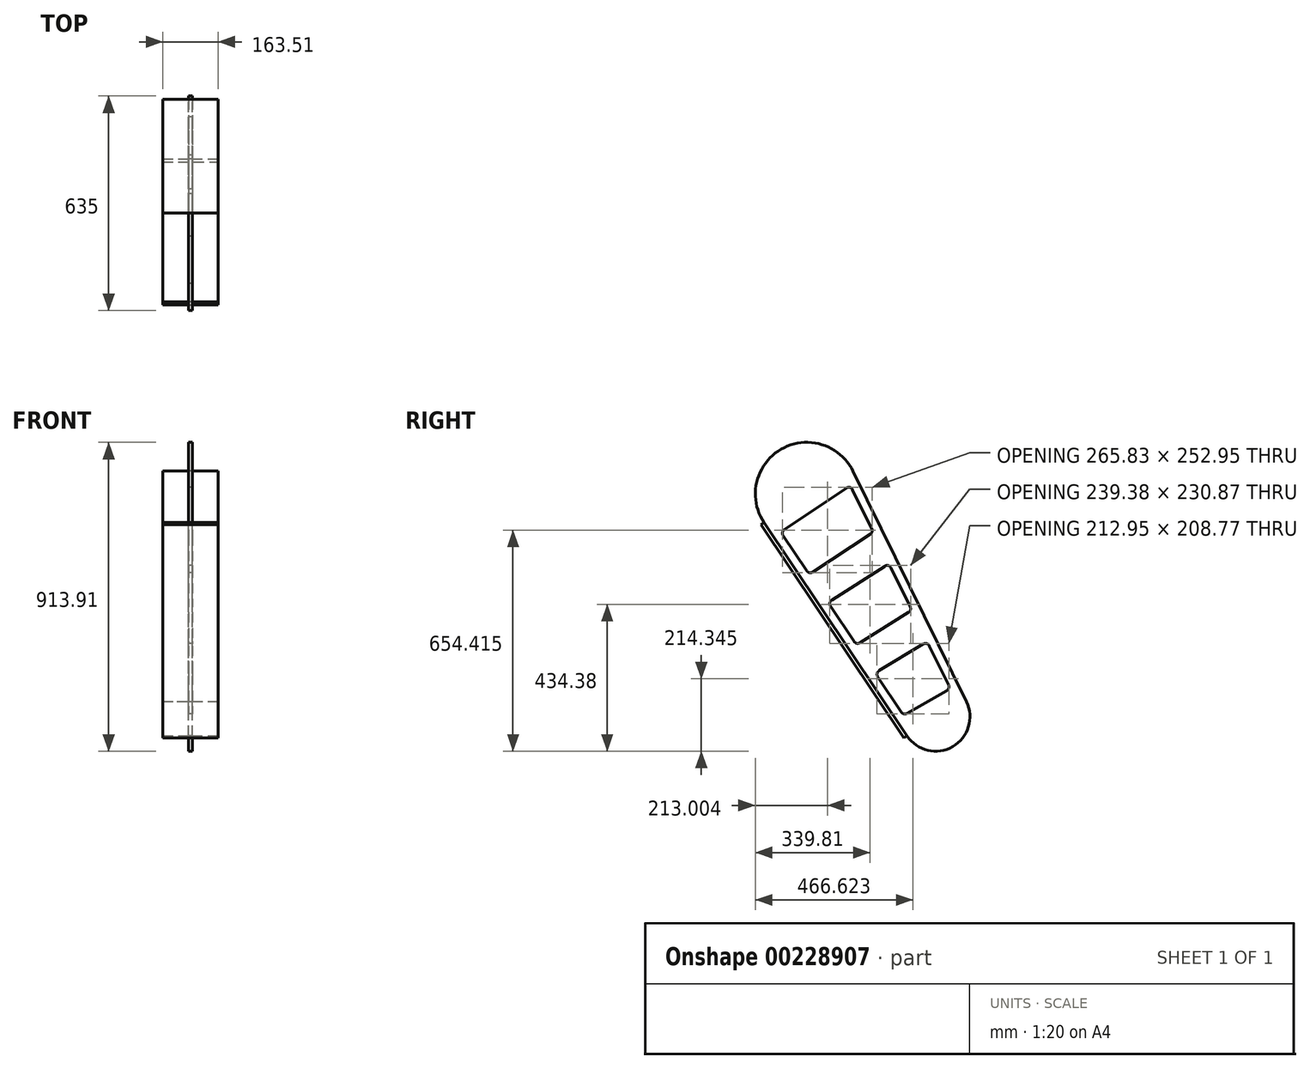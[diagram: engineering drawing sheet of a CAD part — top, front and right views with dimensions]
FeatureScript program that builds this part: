
annotation { "Feature Type Name" : "Feature", "Feature Type Description" : "" }
export const myFeature = defineFeature(function(context is Context, id is Id, definition is map)
    precondition{}
    {
        {
            var Q0;
            Q0=qCreatedBy(makeId("Right.planeOp"),FACE);
            var sketch = newSketch(context, id + "F0", { "sketchPlane" : qUnion([Q0])});
            skCircle(sketch, "E0", {"center": v(-381, 863.11) * mm, "radius": 152.4 * mm, "construction": true});
            skCircle(sketch, "E1", {"center": v(0, 203.2) * mm, "radius": 101.6 * mm, "construction": true});
            skLineSegment(sketch, "E2", {"start": v(91.18, 248.02) * mm, "end": v(-244.23, 930.34) * mm});
            skLineSegment(sketch, "E3", {"start": v(-84.4, 146.65) * mm, "end": v(-507.6, 778.28) * mm});
            skArc(sketch, "E4", {"start": v(-244.23, 930.34) * mm, "mid": v(-457.2, 995.1) * mm, "end": v(-507.6, 778.28) * mm});
            skArc(sketch, "E5", {"start": v(-84.4, 146.65) * mm, "mid": v(50.8, 115.21) * mm, "end": v(91.18, 248.02) * mm});
            skLineSegment(sketch, "E6", {"start": v(-381, 863.11) * mm, "end": v(0, 203.2) * mm, "construction": true});
            skLineSegment(sketch, "E7", {"start": v(-381, 863.11) * mm, "end": v(-228.6, 863.11) * mm, "construction": true});
            skSolve(sketch);
        }
        {
            var Q0;
            Q0=makeQuery(id+"F0.imprint","IMPRINT",FACE,{"disambiguationData":[TD([[makeQuery(id+"F0.imprint","IMPRINT",EDGE,{"derivedFrom":sQuery(id+"F0.wireOp",EDGE,"E2")}),1.0]])]});
            var sketch = newSketch(context, id + "F1", { "sketchPlane" : qUnion([Q0])});
            skArc(sketch, "E8.0", {"start": v(-244.23, 930.34) * mm, "mid": v(-457.2, 995.1) * mm, "end": v(-507.6, 778.28) * mm});
            skLineSegment(sketch, "E8.1", {"start": v(91.18, 248.02) * mm, "end": v(-244.23, 930.34) * mm});
            skArc(sketch, "E8.2", {"start": v(-84.4, 146.65) * mm, "mid": v(50.8, 115.21) * mm, "end": v(91.18, 248.02) * mm});
            skLineSegment(sketch, "E8.3", {"start": v(-84.4, 146.65) * mm, "end": v(-507.6, 778.28) * mm});
            skCircle(sketch, "E9", {"center": v(-440.61, 746.74) * mm, "radius": 12.7 * mm, "construction": true});
            skLineSegment(sketch, "E10", {"start": v(-440.61, 746.74) * mm, "end": v(-90.54, 224.25) * mm, "construction": true});
            skCircle(sketch, "E11.1.0.0", {"center": v(-370.6, 642.24) * mm, "radius": 12.7 * mm, "construction": true});
            skCircle(sketch, "E11.2.0.0", {"center": v(-300.58, 537.74) * mm, "radius": 12.7 * mm, "construction": true});
            skCircle(sketch, "E11.3.0.0", {"center": v(-230.57, 433.24) * mm, "radius": 12.7 * mm, "construction": true});
            skCircle(sketch, "E11.4.0.0", {"center": v(-160.55, 328.75) * mm, "radius": 12.7 * mm, "construction": true});
            skCircle(sketch, "E11.5.0.0", {"center": v(-90.54, 224.25) * mm, "radius": 12.7 * mm, "construction": true});
            skLineSegment(sketch, "E11.direction1", {"start": v(-440.61, 746.74) * mm, "end": v(-370.6, 642.24) * mm, "construction": true});
            skCircle(sketch, "E12", {"center": v(-256.93, 869.8) * mm, "radius": 12.7 * mm, "construction": true});
            skLineSegment(sketch, "E13", {"start": v(-440.61, 746.74) * mm, "end": v(-256.93, 869.8) * mm, "construction": true});
            skLineSegment(sketch, "E14", {"start": v(-256.93, 869.8) * mm, "end": v(27.04, 292.13) * mm, "construction": true});
            skLineSegment(sketch, "E15", {"start": v(27.04, 292.13) * mm, "end": v(-90.54, 224.25) * mm, "construction": true});
            skCircle(sketch, "E16.1.0.0", {"center": v(-200.13, 754.27) * mm, "radius": 12.7 * mm, "construction": true});
            skCircle(sketch, "E16.2.0.0", {"center": v(-143.34, 638.74) * mm, "radius": 12.7 * mm, "construction": true});
            skCircle(sketch, "E16.3.0.0", {"center": v(-86.55, 523.2) * mm, "radius": 12.7 * mm, "construction": true});
            skCircle(sketch, "E16.4.0.0", {"center": v(-29.75, 407.67) * mm, "radius": 12.7 * mm, "construction": true});
            skCircle(sketch, "E16.5.0.0", {"center": v(27.04, 292.13) * mm, "radius": 12.7 * mm, "construction": true});
            skLineSegment(sketch, "E16.direction1", {"start": v(-256.93, 869.8) * mm, "end": v(-200.13, 754.27) * mm, "construction": true});
            skLineSegment(sketch, "E17", {"start": v(-447.68, 757.29) * mm, "end": v(-264, 880.36) * mm});
            skLineSegment(sketch, "E18", {"start": v(-451.16, 739.67) * mm, "end": v(-381.15, 635.17) * mm});
            skLineSegment(sketch, "E19", {"start": v(-363.62, 631.63) * mm, "end": v(-193.16, 743.66) * mm});
            skLineSegment(sketch, "E20", {"start": v(-188.74, 759.87) * mm, "end": v(-245.53, 875.4) * mm});
            skArc(sketch, "E21", {"start": v(-451.16, 739.67) * mm, "mid": v(-453.07, 749.2) * mm, "end": v(-447.68, 757.29) * mm});
            skArc(sketch, "E22", {"start": v(-264, 880.36) * mm, "mid": v(-253.64, 882.07) * mm, "end": v(-245.53, 875.4) * mm});
            skArc(sketch, "E23", {"start": v(-188.74, 759.87) * mm, "mid": v(-187.88, 750.93) * mm, "end": v(-193.16, 743.66) * mm});
            skArc(sketch, "E24", {"start": v(-363.62, 631.63) * mm, "mid": v(-373.11, 629.8) * mm, "end": v(-381.15, 635.17) * mm});
            skLineSegment(sketch, "E25", {"start": v(-307.45, 548.43) * mm, "end": v(-150.2, 649.42) * mm});
            skLineSegment(sketch, "E26", {"start": v(-131.94, 644.34) * mm, "end": v(-75.15, 528.8) * mm});
            skLineSegment(sketch, "E27", {"start": v(-79.82, 512.43) * mm, "end": v(-223.84, 422.47) * mm});
            skLineSegment(sketch, "E28", {"start": v(-241.12, 426.18) * mm, "end": v(-311.13, 530.67) * mm});
            skArc(sketch, "E29", {"start": v(-311.13, 530.67) * mm, "mid": v(-313.02, 540.32) * mm, "end": v(-307.45, 548.43) * mm});
            skArc(sketch, "E30", {"start": v(-150.2, 649.42) * mm, "mid": v(-139.93, 650.97) * mm, "end": v(-131.94, 644.34) * mm});
            skArc(sketch, "E31", {"start": v(-75.15, 528.8) * mm, "mid": v(-74.33, 519.72) * mm, "end": v(-79.82, 512.43) * mm});
            skArc(sketch, "E32", {"start": v(-223.84, 422.47) * mm, "mid": v(-233.23, 420.83) * mm, "end": v(-241.12, 426.18) * mm});
            skLineSegment(sketch, "E33", {"start": v(-167.11, 339.62) * mm, "end": v(-36.31, 418.54) * mm});
            skLineSegment(sketch, "E34", {"start": v(-18.36, 413.27) * mm, "end": v(38.44, 297.74) * mm});
            skLineSegment(sketch, "E35", {"start": v(33.39, 281.14) * mm, "end": v(-84.19, 213.25) * mm});
            skLineSegment(sketch, "E36", {"start": v(-101.1, 217.18) * mm, "end": v(-171.1, 321.68) * mm});
            skArc(sketch, "E37", {"start": v(-171.1, 321.68) * mm, "mid": v(-172.95, 331.5) * mm, "end": v(-167.11, 339.62) * mm});
            skArc(sketch, "E38", {"start": v(-36.31, 418.54) * mm, "mid": v(-26.18, 419.85) * mm, "end": v(-18.36, 413.27) * mm});
            skArc(sketch, "E39", {"start": v(38.44, 297.74) * mm, "mid": v(39.2, 288.44) * mm, "end": v(33.39, 281.14) * mm});
            skArc(sketch, "E40", {"start": v(-84.19, 213.25) * mm, "mid": v(-93.42, 211.88) * mm, "end": v(-101.1, 217.18) * mm});
            skSolve(sketch);
        }
        {
            var Q0;
            Q0 = qSketchRegion(id + "F1", true);
            extrude(context, id + "F2", {"entities" : qUnion([Q0]), "depth" : 11.1 * mm});
        }
        {
            var Q0;
            Q0=makeQuery(id+"F2.opExtrude","SWEPT_FACE",FACE,{"disambiguationData":[OSD([sQuery(id+"F1.wireOp",EDGE,"E8.1")])]});
            var sketch = newSketch(context, id + "F3", { "sketchPlane" : qUnion([Q0])});
            skLineSegment(sketch, "E41.bottom", {"start": v(-87.31, 942.66) * mm, "end": v(76.2, 942.66) * mm});
            skLineSegment(sketch, "E41.top", {"start": v(-87.31, 182.36) * mm, "end": v(76.2, 182.36) * mm});
            skLineSegment(sketch, "E41.left", {"start": v(-87.31, 942.66) * mm, "end": v(-87.31, 182.36) * mm});
            skLineSegment(sketch, "E41.right", {"start": v(76.2, 942.66) * mm, "end": v(76.2, 182.36) * mm});
            skSolve(sketch);
        }
        {
            var Q0;
            {var subQ2=sQuery(id+"F3.wireOp",EDGE,"E41.left");Q0=makeQuery(id+"F3.imprint","IMPRINT",FACE,{"disambiguationData":[TD([[makeQuery(id+"F3.imprint","IMPRINT",EDGE,{"derivedFrom":subQ2}),1.0]])]});}
            var Q1;
            {var subQ2=sQuery(id+"F3.wireOp",EDGE,"E41.right");Q1=makeQuery(id+"F3.imprint","IMPRINT",FACE,{"disambiguationData":[TD([[makeQuery(id+"F3.imprint","IMPRINT",EDGE,{"derivedFrom":subQ2}),-1.0]])]});}
            var Q2;
            {var subQ1=sQuery(id+"F1.wireOp",EDGE,"E8.1");var subQ2=makeQuery(id+"F2.opExtrude","CAP_EDGE",EDGE,{"disambiguationData":[OSD([subQ1])],"isStart":true});Q2=makeQuery(id+"F3.imprint","IMPRINT",FACE,{"disambiguationData":[TD([[makeQuery(id+"F3.imprint","IMPRINT",EDGE,{"derivedFrom":subQ2}),1.0]])]});}
            extrude(context, id + "F4", {"entities" : qUnion([Q0, Q1, Q2]), "operationType" : NewBodyOperationType.ADD, "depth" : 7 / 406.4 * mm});
        }
        {
            var Q0;
            Q0=makeQuery(id+"F2.opExtrude","SWEPT_FACE",FACE,{"disambiguationData":[OSD([sQuery(id+"F1.wireOp",EDGE,"E8.3")])]});
            var sketch = newSketch(context, id + "F5", { "sketchPlane" : qUnion([Q0])});
            skLineSegment(sketch, "E42.bottom", {"start": v(-76.2, 929.12) * mm, "end": v(87.31, 929.12) * mm});
            skLineSegment(sketch, "E42.top", {"start": v(-76.2, 168.81) * mm, "end": v(87.31, 168.81) * mm});
            skLineSegment(sketch, "E42.left", {"start": v(-76.2, 929.12) * mm, "end": v(-76.2, 168.81) * mm});
            skLineSegment(sketch, "E42.right", {"start": v(87.31, 929.12) * mm, "end": v(87.31, 168.81) * mm});
            skSolve(sketch);
        }
        {
            var Q0;
            {var subQ2=sQuery(id+"F5.wireOp",EDGE,"E42.left");Q0=makeQuery(id+"F5.imprint","IMPRINT",FACE,{"disambiguationData":[TD([[makeQuery(id+"F5.imprint","IMPRINT",EDGE,{"derivedFrom":subQ2}),1.0]])]});}
            var Q1;
            {var subQ2=sQuery(id+"F5.wireOp",EDGE,"E42.right");Q1=makeQuery(id+"F5.imprint","IMPRINT",FACE,{"disambiguationData":[TD([[makeQuery(id+"F5.imprint","IMPRINT",EDGE,{"derivedFrom":subQ2}),-1.0]])]});}
            var Q2;
            {var subQ1=sQuery(id+"F1.wireOp",EDGE,"E8.3");var subQ2=makeQuery(id+"F2.opExtrude","CAP_EDGE",EDGE,{"disambiguationData":[OSD([subQ1])],"isStart":true});Q2=makeQuery(id+"F5.imprint","IMPRINT",FACE,{"disambiguationData":[TD([[makeQuery(id+"F5.imprint","IMPRINT",EDGE,{"derivedFrom":subQ2}),-1.0]])]});}
            extrude(context, id + "F6", {"entities" : qUnion([Q0, Q1, Q2]), "operationType" : NewBodyOperationType.ADD, "depth" : 11.1 * mm});
        }
    });
